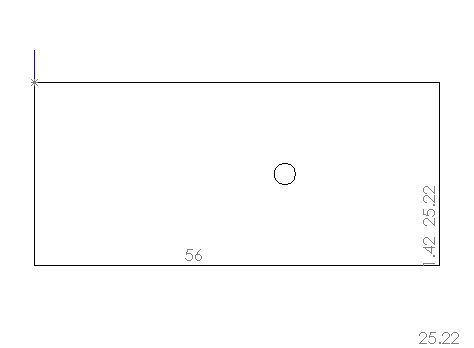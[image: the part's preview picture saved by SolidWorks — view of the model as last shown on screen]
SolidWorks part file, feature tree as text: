
SOLIDWORKS PART (.sldprt)
format: sldprt  version: not decoded by parser v0  size: 116,736 bytes
history: native  units: mm
features: sketch x5, cut_extrude x4, material x1, extrude x1 + 1 further entry (+14 scaffold rows collapsed)
feature tree (26):
  scaffold x14  (default folders/planes/origin — collapsed)
  material  "Material <not specified>"
  "Annotations"  RD1=25.22mm RD2=25.22mm RD3=1.42mm RD4=1.42mm RD5=56mm
  sketch  "Sketch1"
  extrude  "Extrude1"  Depth=56mm
  sketch  "Sketch2"  dims[D1=~4.490128mm]
  cut_extrude  "Cut-Extrude1"  [1 undecoded]
  sketch  "Sketch3"  dims[D1=~11.339659mm]
  cut_extrude  "Cut-Extrude2"  [1 undecoded]
  sketch  "Sketch4"  dims[D1=1.5875mm]
  cut_extrude  "Cut-Extrude3"  [1 undecoded]
  sketch  "Sketch5"  dims[D1=~2.245064mm]
  cut_extrude  "Cut-Extrude4"  [1 undecoded]
decode coverage: 5 of 10 modeling features carry decoded parameters; 1 rows unclassified (native names shown)
note: ~ marks probable driven/reference dimensions
note: 4 parameter values undecoded
summary: no parameter record found for 4 features
note: suppression state not decoded; provenance and decode notes live in map.json
